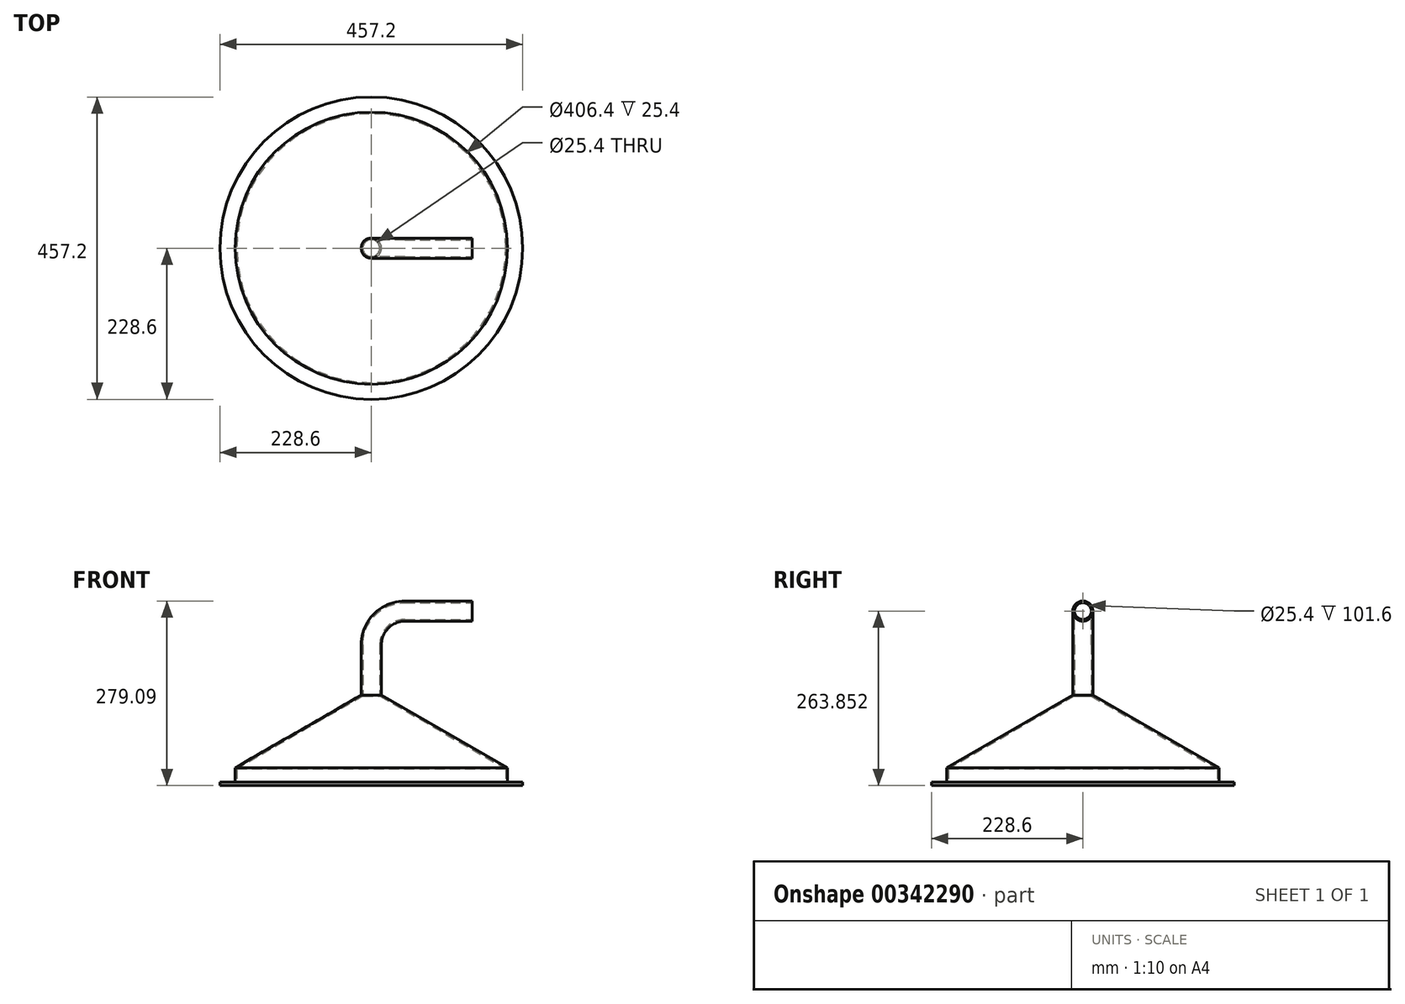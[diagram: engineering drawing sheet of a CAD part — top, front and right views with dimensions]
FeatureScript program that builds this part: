
annotation { "Feature Type Name" : "Feature", "Feature Type Description" : "" }
export const myFeature = defineFeature(function(context is Context, id is Id, definition is map)
    precondition{}
    {
        {
            var Q0;
            Q0=qCreatedBy(makeId("Front.planeOp"),FACE);
            var sketch = newSketch(context, id + "F0", { "sketchPlane" : qUnion([Q0])});
            skLineSegment(sketch, "E0", {"start": v(203.2, 0) * mm, "end": v(228.6, 0) * mm});
            skLineSegment(sketch, "E1", {"start": v(228.6, 0) * mm, "end": v(228.6, 5.08) * mm});
            skLineSegment(sketch, "E2", {"start": v(228.6, 5.08) * mm, "end": v(205.74, 5.08) * mm});
            skLineSegment(sketch, "E3", {"start": v(12.7, 135.39) * mm, "end": v(203.2, 25.4) * mm});
            skLineSegment(sketch, "E4", {"start": v(203.2, 25.4) * mm, "end": v(203.2, 0) * mm});
            skLineSegment(sketch, "E5", {"start": v(0, 0) * mm, "end": v(0, 95.24) * mm, "construction": true});
            skLineSegment(sketch, "E6", {"start": v(12.7, 135.39) * mm, "end": v(12.7, 136.85) * mm});
            skLineSegment(sketch, "E7", {"start": v(12.7, 136.85) * mm, "end": v(15.24, 136.85) * mm});
            skLineSegment(sketch, "E8", {"start": v(205.74, 5.08) * mm, "end": v(205.74, 26.87) * mm});
            skLineSegment(sketch, "E9", {"start": v(205.74, 26.87) * mm, "end": v(15.24, 136.85) * mm});
            skSolve(sketch);
        }
        {
            var Q0;
            Q0 = qSketchRegion(id + "F0", true);
            var Q1;
            Q1=sQuery(id+"F0.wireOp",EDGE,"E5");
            revolve(context, id + "F1", {"entities" : qUnion([Q0]), "axis" : qUnion([Q1]), "revolveType" : RevolveType.FULL});
        }
        {
            var Q0;
            Q0=qCreatedBy(makeId("Front.planeOp"),FACE);
            var sketch = newSketch(context, id + "F2", { "sketchPlane" : qUnion([Q0])});
            skLineSegment(sketch, "E10", {"start": v(0, 136.85) * mm, "end": v(0, 213.05) * mm});
            skArc(sketch, "E11", {"start": v(50.8, 263.85) * mm, "mid": v(14.88, 248.97) * mm, "end": v(0, 213.05) * mm});
            skLineSegment(sketch, "E12", {"start": v(50.8, 263.85) * mm, "end": v(152.4, 263.85) * mm});
            skSolve(sketch);
        }
        {
            var Q0;
            Q0=makeQuery(id+"F1.opRevolve","SWEPT_FACE",FACE,{"disambiguationData":[OSD([sQuery(id+"F0.wireOp",EDGE,"E7")])]});
            var Q1;
            Q1 = qConstructionFilter(qBodyType(qCreatedBy(id + "F2" ,EDGE), BodyType.WIRE), ConstructionObject.NO);
            sweep(context, id + "F3", {"operationType" : NewBodyOperationType.ADD, "profiles" : qUnion([Q0]), "path" : qUnion([Q1])});
        }
    });
